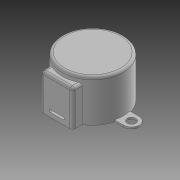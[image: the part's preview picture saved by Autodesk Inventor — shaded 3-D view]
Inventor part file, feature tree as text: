
AUTODESK INVENTOR PART (.ipt)
format: ipt  version: 2017 (Build 210142000, 142)  size: 195,584 bytes
history: native  units: mm
features: extrude x7, sketch x2, fillet x1
ambient origin geometry x8: Origin, YZ Plane, XZ Plane, XY Plane, X Axis, Y Axis, Z Axis, Center Point
bodies: Solid1 (feature_tree)
feature tree (10):
  sketch  "Sketch1"  dims[d0=13.95mm d1=7.18mm]
  extrude  "Extrusion1"  Depth=13.95mm
  extrude  "Extrusion2"  Depth=2.0mm
  extrude  "Extrusion3"  Depth=2.0mm
  extrude  "Extrusion4"  Depth=19.2mm TaperAngle=0.0deg
  extrude  "Extrusion5"  Depth=2.0mm TaperAngle=0.0deg
  extrude  "Extrusion6"  Depth=2.0mm TaperAngle=0.0deg
  fillet  "Fillet1"  Radius=9.22mm
  extrude  "Extrusion7"  Depth=2.0mm
  sketch  "Sketch2"  dims[d2=4.46mm d3=3.5mm d4=4.0mm d5=19.2mm d6=0.0mm d7=0.79mm d8=0.0mm d9=16.5mm d10=0.0mm d11=9.22mm d12=5.0mm d13=2.85mm d14=1.75mm d15=0.0mm d16=3.78mm d17=0.0mm d18=9.73mm d19=0.0mm d20=1.2mm d21=2.0mm d22=1.12mm d23=6.0mm d24=2.0mm d25=0.0mm d26=35.5mm d27=6.0mm]
